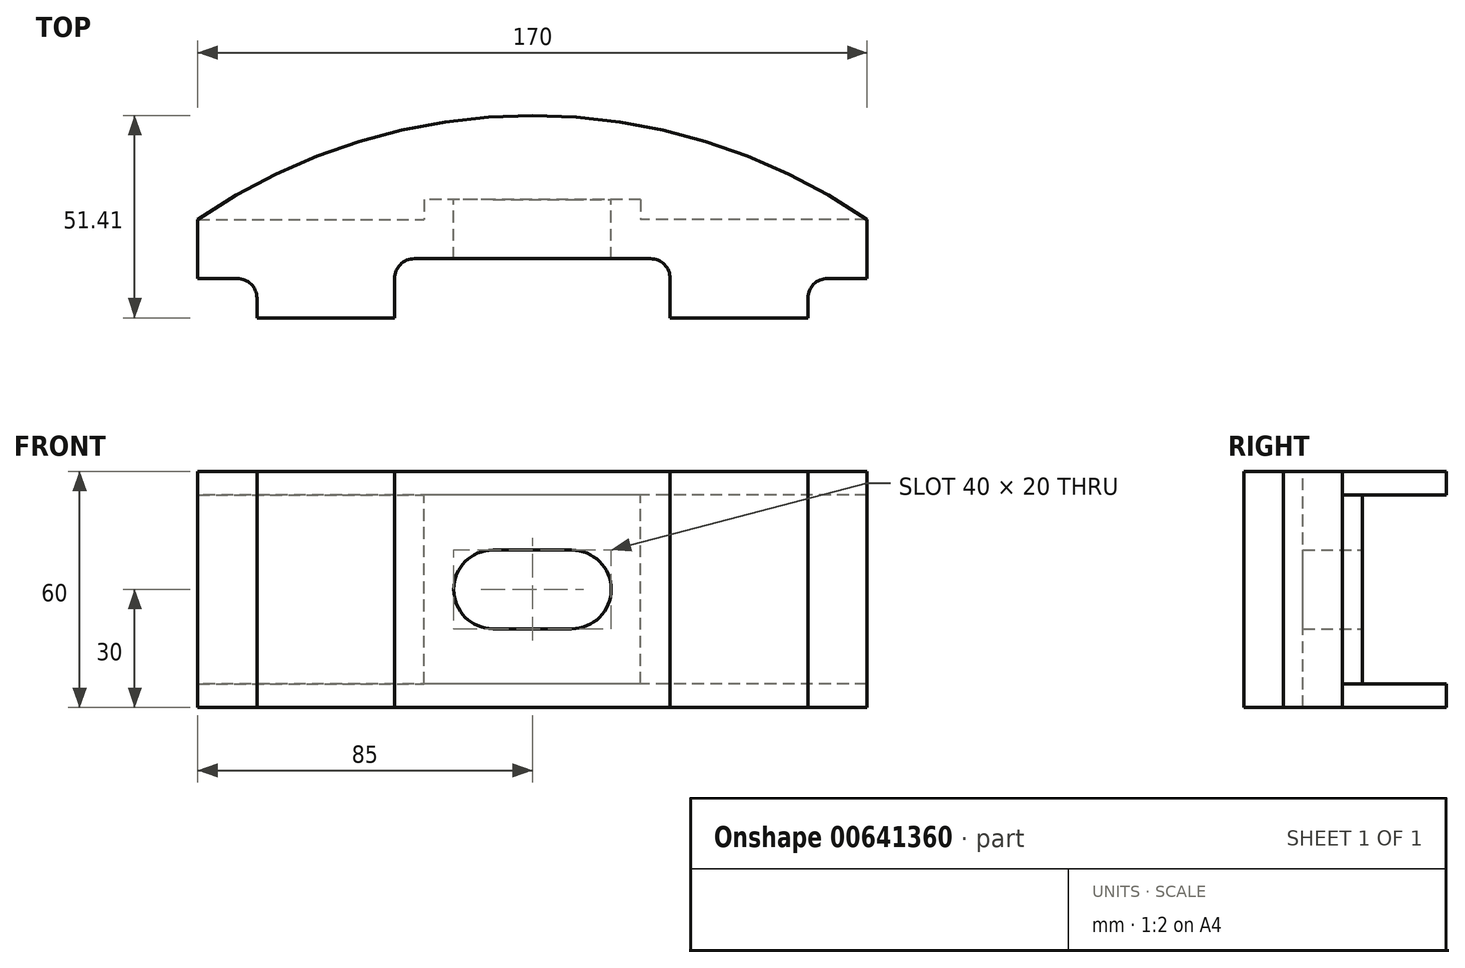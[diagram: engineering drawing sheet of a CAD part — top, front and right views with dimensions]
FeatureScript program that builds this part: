
annotation { "Feature Type Name" : "Feature", "Feature Type Description" : "" }
export const myFeature = defineFeature(function(context is Context, id is Id, definition is map)
    precondition{}
    {
        {
            var Q0;
            Q0=qCreatedBy(makeId("Front.planeOp"),FACE);
            var sketch = newSketch(context, id + "F0", { "sketchPlane" : qUnion([Q0])});
            skLineSegment(sketch, "E0.rect.bottom", {"start": v(85, 30) * mm, "end": v(-85, 30) * mm});
            skLineSegment(sketch, "E0.rect.top", {"start": v(85, -30) * mm, "end": v(-85, -30) * mm});
            skLineSegment(sketch, "E0.rect.left", {"start": v(85, 30) * mm, "end": v(85, -30) * mm});
            skLineSegment(sketch, "E0.rect.right", {"start": v(-85, 30) * mm, "end": v(-85, -30) * mm});
            skPoint(sketch, "E0.rect.middle", {"position": v(0, 0) * mm});
            skSolve(sketch);
        }
        {
            var Q0;
            Q0=qSketchRegion(id+"F0",true);
            extrude(context, id + "F1", {"entities" : qUnion([Q0]), "depth" : 30 * mm});
        }
        {
            var Q0;
            Q0=qCreatedBy(makeId("Top.planeOp"),FACE);
            var sketch = newSketch(context, id + "F2", { "sketchPlane" : qUnion([Q0])});
            skLineSegment(sketch, "E1.rect.bottom", {"start": v(35, -15) * mm, "end": v(-35, -15) * mm});
            skLineSegment(sketch, "E1.rect.top", {"start": v(35, -45) * mm, "end": v(-35, -45) * mm});
            skLineSegment(sketch, "E1.rect.left", {"start": v(35, -15) * mm, "end": v(35, -45) * mm});
            skLineSegment(sketch, "E1.rect.right", {"start": v(-35, -15) * mm, "end": v(-35, -45) * mm});
            skPoint(sketch, "E1.rect.middle", {"position": v(0, -30) * mm});
            skPoint(sketch, "E2.rect.middle", {"position": v(17.94, 30.97) * mm});
            skSolve(sketch);
        }
        {
            var Q0;
            Q0=makeQuery(id+"F2.imprint","IMPRINT",FACE,{"disambiguationData":[TD([[makeQuery(id+"F2.imprint","IMPRINT",EDGE,{"derivedFrom":sQuery(id+"F2.wireOp",EDGE,"E1.rect.bottom")}),1.0]])]});
            extrude(context, id + "F3", {"entities" : qUnion([Q0]), "operationType" : NewBodyOperationType.REMOVE, "oppositeDirection" : true, "depth" : 119.38 * mm, "symmetric" : true});
        }
        {
            var Q0;
            Q0=makeQuery(id+"F3.boolean.opBoolean","COPY",EDGE,{"derivedFrom":makeQuery(id+"F3.opExtrude","SWEPT_EDGE",EDGE,{"disambiguationData":[OSD([sQuery(id+"F2.wireOp",EDGE,"E1.rect.bottom"),sQuery(id+"F2.wireOp",EDGE,"E1.rect.left")])]})});
            var Q1;
            Q1=makeQuery(id+"F3.boolean.opBoolean","COPY",EDGE,{"derivedFrom":makeQuery(id+"F3.opExtrude","SWEPT_EDGE",EDGE,{"disambiguationData":[OSD([sQuery(id+"F2.wireOp",EDGE,"E1.rect.bottom"),sQuery(id+"F2.wireOp",EDGE,"E1.rect.right")])]})});
            fillet(context, id + "F4", {"entities" : qUnion([Q0, Q1]), "radius" : 5 * mm, "tangentPropagation" : true, "allowEdgeOverflow" : false});
        }
        {
            var Q0;
            Q0=makeQuery(id+"F1.opExtrude","SWEPT_FACE",FACE,{"disambiguationData":[OSD([sQuery(id+"F0.wireOp",EDGE,"E0.rect.bottom")])]});
            var sketch = newSketch(context, id + "F5", { "sketchPlane" : qUnion([Q0])});
            skLineSegment(sketch, "E3.bottom", {"start": v(85, -30) * mm, "end": v(70, -30) * mm});
            skLineSegment(sketch, "E3.top", {"start": v(85, -20) * mm, "end": v(75, -20) * mm});
            skLineSegment(sketch, "E3.left", {"start": v(85, -30) * mm, "end": v(85, -20) * mm});
            skLineSegment(sketch, "E3.right", {"start": v(70, -30) * mm, "end": v(70, -25) * mm});
            skLineSegment(sketch, "E4.bottom", {"start": v(-85, -30) * mm, "end": v(-70, -30) * mm});
            skLineSegment(sketch, "E4.top", {"start": v(-85, -20) * mm, "end": v(-75, -20) * mm});
            skLineSegment(sketch, "E4.left", {"start": v(-85, -30) * mm, "end": v(-85, -20) * mm});
            skLineSegment(sketch, "E4.right", {"start": v(-70, -30) * mm, "end": v(-70, -25) * mm});
            skPoint(sketch, "E5.visualSharp", {"position": v(70, -20) * mm});
            skArc(sketch, "E5.filletArc", {"start": v(75, -20) * mm, "mid": v(71.46, -21.46) * mm, "end": v(70, -25) * mm});
            skPoint(sketch, "E6.visualSharp", {"position": v(-70, -20) * mm});
            skArc(sketch, "E6.filletArc", {"start": v(-70, -25) * mm, "mid": v(-71.46, -21.46) * mm, "end": v(-75, -20) * mm});
            skSolve(sketch);
        }
        {
            var Q0;
            Q0=qSketchRegion(id+"F5",true);
            extrude(context, id + "F6", {"entities" : qUnion([Q0]), "operationType" : NewBodyOperationType.REMOVE, "endBound" : BoundingType.THROUGH_ALL, "oppositeDirection" : true, "depth" : 25 * mm});
        }
        {
            var Q0;
            Q0=makeQuery(id+"F1.opExtrude","SWEPT_FACE",FACE,{"disambiguationData":[OSD([sQuery(id+"F0.wireOp",EDGE,"E0.rect.bottom")])]});
            var sketch = newSketch(context, id + "F7", { "sketchPlane" : qUnion([Q0])});
            skLineSegment(sketch, "E7.bottom", {"start": v(85, 0) * mm, "end": v(27.5, 0) * mm});
            skLineSegment(sketch, "E7.top", {"start": v(85, -5) * mm, "end": v(27.5, -5) * mm});
            skLineSegment(sketch, "E7.left", {"start": v(85, 0) * mm, "end": v(85, -5) * mm});
            skLineSegment(sketch, "E7.right", {"start": v(27.5, 0) * mm, "end": v(27.5, -5) * mm});
            skLineSegment(sketch, "E8.bottom", {"start": v(-85, 0) * mm, "end": v(-27.5, 0) * mm});
            skLineSegment(sketch, "E8.top", {"start": v(-85, -5) * mm, "end": v(-27.5, -5) * mm});
            skLineSegment(sketch, "E8.left", {"start": v(-85, 0) * mm, "end": v(-85, -5) * mm});
            skLineSegment(sketch, "E8.right", {"start": v(-27.5, 0) * mm, "end": v(-27.5, -5) * mm});
            skSolve(sketch);
        }
        {
            var Q0;
            Q0=qSketchRegion(id+"F7",true);
            extrude(context, id + "F8", {"entities" : qUnion([Q0]), "operationType" : NewBodyOperationType.REMOVE, "endBound" : BoundingType.THROUGH_ALL, "oppositeDirection" : true, "depth" : 25 * mm});
        }
        {
            var Q0;
            Q0=makeQuery(id+"F1.opExtrude","SWEPT_FACE",FACE,{"disambiguationData":[OSD([sQuery(id+"F0.wireOp",EDGE,"E0.rect.bottom")])]});
            var sketch = newSketch(context, id + "F9", { "sketchPlane" : qUnion([Q0])});
            skArc(sketch, "E9", {"start": v(85, -5) * mm, "mid": v(0, 21.4) * mm, "end": v(-85, -5) * mm});
            skSolve(sketch);
        }
        {
            var Q0;
            Q0=makeQuery(id+"F9.imprint","IMPRINT",FACE,{"disambiguationData":[TD([[makeQuery(id+"F9.imprint","IMPRINT",EDGE,{"derivedFrom":sQuery(id+"F9.wireOp",EDGE,"E9")}),1.0]])]});
            extrude(context, id + "F10", {"entities" : qUnion([Q0]), "operationType" : NewBodyOperationType.ADD, "oppositeDirection" : true, "depth" : 6 * mm});
        }
        {
            var Q0;
            Q0=makeQuery(id+"F1.opExtrude","SWEPT_BODY",BODY,{"disambiguationData":[OSD([sQuery(id+"F0.wireOp",EDGE,"E0.rect.bottom"),sQuery(id+"F0.wireOp",EDGE,"E0.rect.top"),sQuery(id+"F0.wireOp",EDGE,"E0.rect.left"),sQuery(id+"F0.wireOp",EDGE,"E0.rect.right")])]});
            var Q1;
            {var subQ0=sQuery(id+"F0.wireOp",EDGE,"E0.rect.bottom");Q1=makeQuery(id+"F10.boolean.opBoolean","MERGE",FACE,{"derivedFrom":[makeQuery(id+"F1.opExtrude","SWEPT_FACE",FACE,{"disambiguationData":[OSD([subQ0])]}),makeQuery(id+"F10.opExtrude","CAP_FACE",FACE,{"disambiguationData":[OSD([subQ0,sQuery(id+"F7.wireOp",EDGE,"E7.top"),sQuery(id+"F7.wireOp",EDGE,"E7.right"),sQuery(id+"F7.wireOp",EDGE,"E8.top"),sQuery(id+"F7.wireOp",EDGE,"E8.right"),sQuery(id+"F9.wireOp",EDGE,"E9")])],"isStart":true})]});}
            var Q2;
            Q2=qCreatedBy(makeId("Top.planeOp"),FACE);
            mirror(context, id + "F11", {"operationType" : NewBodyOperationType.ADD, "entities" : qUnion([Q0]), "faces" : qUnion([Q1]), "mirrorPlane" : qUnion([Q2])});
        }
        {
            var Q0;
            Q0=makeQuery(id+"F1.opExtrude","CAP_FACE",FACE,{"disambiguationData":[OSD([sQuery(id+"F0.wireOp",EDGE,"E0.rect.bottom"),sQuery(id+"F0.wireOp",EDGE,"E0.rect.top"),sQuery(id+"F0.wireOp",EDGE,"E0.rect.left"),sQuery(id+"F0.wireOp",EDGE,"E0.rect.right")])],"isStart":true});
            var sketch = newSketch(context, id + "F12", { "sketchPlane" : qUnion([Q0])});
            skLineSegment(sketch, "E10.rect.bottom", {"start": v(10, 10) * mm, "end": v(-10, 10) * mm});
            skLineSegment(sketch, "E10.rect.top", {"start": v(10, -10) * mm, "end": v(-10, -10) * mm});
            skLineSegment(sketch, "E10.rect.left", {"start": v(20, 0) * mm, "end": v(20, 0) * mm});
            skLineSegment(sketch, "E10.rect.right", {"start": v(-20, 0) * mm, "end": v(-20, 0) * mm});
            skPoint(sketch, "E10.rect.middle", {"position": v(0, 0) * mm});
            skPoint(sketch, "E11.visualSharp", {"position": v(20, 10) * mm});
            skArc(sketch, "E11.filletArc", {"start": v(20, 0) * mm, "mid": v(17.07, 7.07) * mm, "end": v(10, 10) * mm});
            skPoint(sketch, "E12.visualSharp", {"position": v(-20, 10) * mm});
            skArc(sketch, "E12.filletArc", {"start": v(-10, 10) * mm, "mid": v(-17.07, 7.07) * mm, "end": v(-20, 0) * mm});
            skPoint(sketch, "E13.visualSharp", {"position": v(-20, -10) * mm});
            skArc(sketch, "E13.filletArc", {"start": v(-20, 0) * mm, "mid": v(-17.07, -7.07) * mm, "end": v(-10, -10) * mm});
            skPoint(sketch, "E14.visualSharp", {"position": v(20, -10) * mm});
            skArc(sketch, "E14.filletArc", {"start": v(10, -10) * mm, "mid": v(17.07, -7.07) * mm, "end": v(20, 0) * mm});
            skSolve(sketch);
        }
        {
            var Q0;
            Q0=qSketchRegion(id+"F12",true);
            extrude(context, id + "F13", {"entities" : qUnion([Q0]), "operationType" : NewBodyOperationType.REMOVE, "endBound" : BoundingType.THROUGH_ALL, "oppositeDirection" : true, "depth" : 25 * mm});
        }
    });
